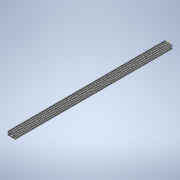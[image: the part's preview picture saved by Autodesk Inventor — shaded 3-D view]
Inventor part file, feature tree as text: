
AUTODESK INVENTOR PART (.ipt)
format: ipt  version: 2020 (Build 240168000, 168)  size: 345,088 bytes
history: native  units: in
note: dims shown in document units (in); Inventor stores cm internally (conversion verified against a paired STEP export)
features: sketch x2, extrude x1
ambient origin geometry x8: Origin, YZ Plane, XZ Plane, XY Plane, X Axis, Y Axis, Z Axis, Center Point
bodies: Solid1 (feature_tree)
feature tree (3):
  extrude  "Extrusion1"  [1 undecoded]
  sketch  "Sketch2"
  sketch  "Sketch1"  dims[d0=40.0in d1=0.0in]
note: 1 required parameter value undecoded (feature->parameter linkage not recoverable at this tier; creation-order binding heuristic only, values carry confidence <= 0.55)
